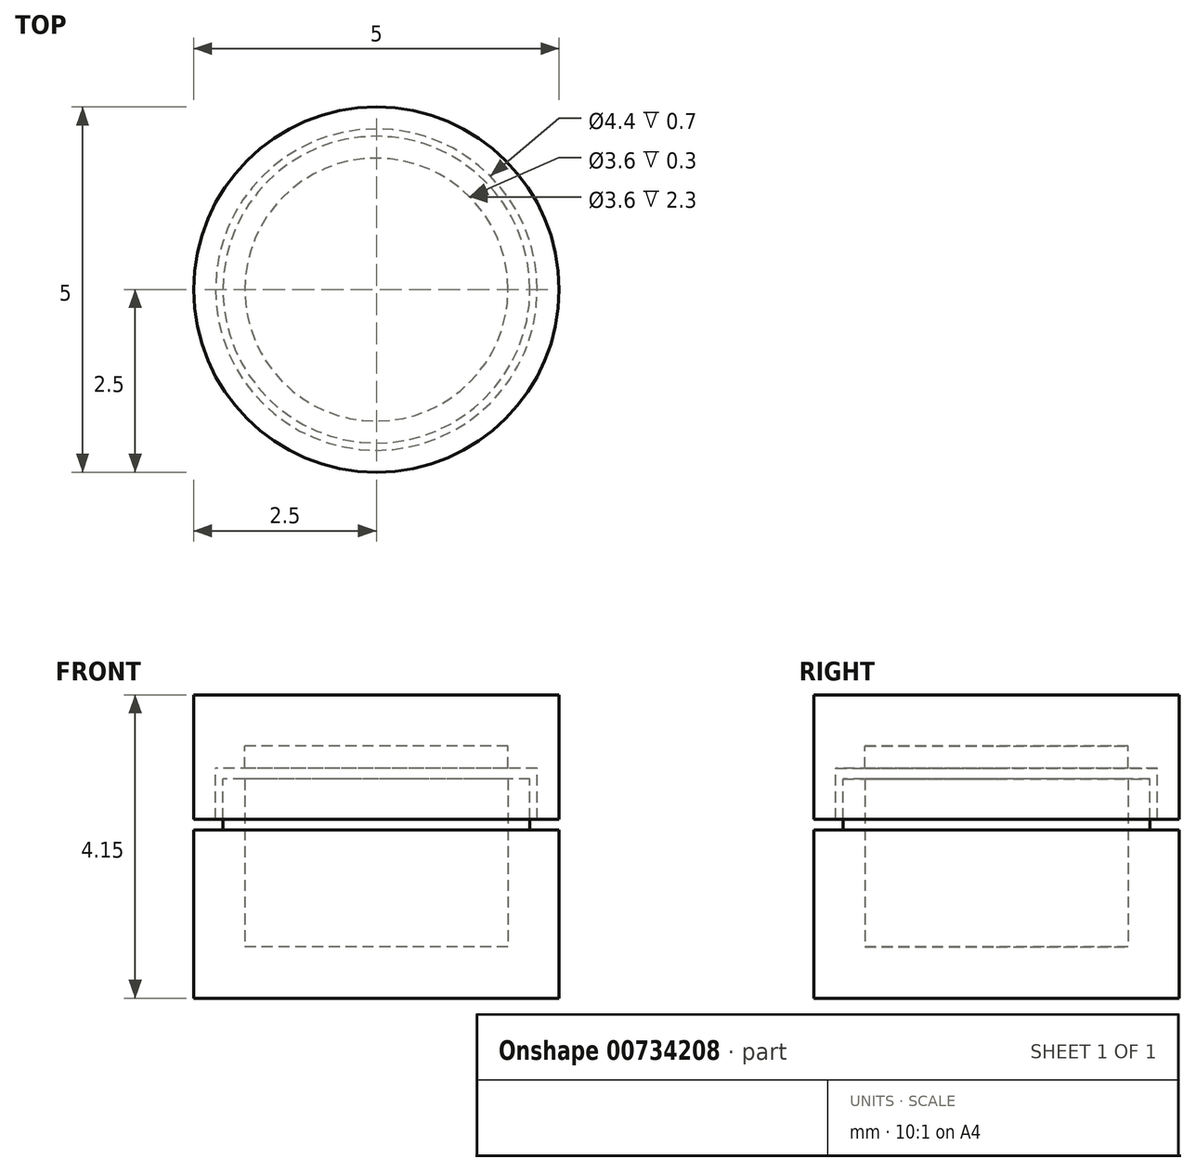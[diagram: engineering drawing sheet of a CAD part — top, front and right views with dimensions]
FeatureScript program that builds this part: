
annotation { "Feature Type Name" : "Feature", "Feature Type Description" : "" }
export const myFeature = defineFeature(function(context is Context, id is Id, definition is map)
    precondition{}
    {
        {
            var Q0;
            Q0=qCreatedBy(makeId("Top.planeOp"),FACE);
            var sketch = newSketch(context, id + "F0", { "sketchPlane" : qUnion([Q0])});
            skCircle(sketch, "E0", {"center": v(0, 0) * mm, "radius": 2.5 * mm});
            skCircle(sketch, "E1", {"center": v(0, 0) * mm, "radius": 1.8 * mm});
            skSolve(sketch);
        }
        {
            var Q0;
            Q0=makeQuery(id+"F0.imprint","IMPRINT",FACE,{"disambiguationData":[TD([[makeQuery(id+"F0.imprint","IMPRINT",EDGE,{"derivedFrom":sQuery(id+"F0.wireOp",EDGE,"E0")}),1.0]])]});
            extrude(context, id + "F1", {"entities" : qUnion([Q0]), "depth" : 3 * mm, "offsetDistance" : 25.4 * mm});
        }
        {
            var Q0;
            Q0=makeQuery(id+"F0.imprint","IMPRINT",FACE,{"disambiguationData":[TD([[makeQuery(id+"F0.imprint","IMPRINT",EDGE,{"derivedFrom":sQuery(id+"F0.wireOp",EDGE,"E1")}),1.0]])]});
            extrude(context, id + "F2", {"entities" : qUnion([Q0]), "operationType" : NewBodyOperationType.ADD, "depth" : 0.7 * mm, "offsetDistance" : 25.4 * mm});
        }
        {
            var Q0;
            Q0=makeQuery(id+"F1.opExtrude","CAP_FACE",FACE,{"disambiguationData":[OSD([sQuery(id+"F0.wireOp",EDGE,"E0"),sQuery(id+"F0.wireOp",EDGE,"E1")])],"isStart":false});
            var sketch = newSketch(context, id + "F3", { "sketchPlane" : qUnion([Q0])});
            skCircle(sketch, "E2.0", {"center": v(0, 0) * mm, "radius": 2.5 * mm});
            skCircle(sketch, "E3", {"center": v(0, 0) * mm, "radius": 2.1 * mm});
            skSolve(sketch);
        }
        {
            var Q0;
            Q0 = qSketchRegion(id + "F3", true);
            extrude(context, id + "F4", {"entities" : qUnion([Q0]), "operationType" : NewBodyOperationType.REMOVE, "oppositeDirection" : true, "depth" : 0.7 * mm, "offsetDistance" : 25.4 * mm});
        }
        {
            var Q0;
            Q0=qCreatedBy(makeId("Front.planeOp"),FACE);
            var sketch = newSketch(context, id + "F5", { "sketchPlane" : qUnion([Q0])});
            skLineSegment(sketch, "E4", {"start": v(-2.5, 2.45) * mm, "end": v(-2.5, 4.15) * mm});
            skLineSegment(sketch, "E5", {"start": v(-2.5, 4.15) * mm, "end": v(0, 4.15) * mm});
            skLineSegment(sketch, "E6", {"start": v(0, 4.15) * mm, "end": v(0, 0) * mm});
            skLineSegment(sketch, "E7", {"start": v(-2.5, 2.45) * mm, "end": v(-2.2, 2.45) * mm});
            skLineSegment(sketch, "E8", {"start": v(-2.2, 2.45) * mm, "end": v(-2.2, 3.15) * mm});
            skLineSegment(sketch, "E9", {"start": v(-2.2, 3.15) * mm, "end": v(-1.8, 3.15) * mm});
            skLineSegment(sketch, "E10", {"start": v(-1.8, 3.15) * mm, "end": v(-1.8, 3.45) * mm});
            skLineSegment(sketch, "E11", {"start": v(-1.8, 3.45) * mm, "end": v(0, 3.45) * mm});
            skSolve(sketch);
        }
        {
            var Q0;
            Q0=makeQuery(id+"F5.imprint","IMPRINT",FACE,{"disambiguationData":[TD([[makeQuery(id+"F5.imprint","IMPRINT",EDGE,{"derivedFrom":sQuery(id+"F5.wireOp",EDGE,"E4")}),-1.0]])]});
            var Q1;
            Q1=sQuery(id+"F5.wireOp",EDGE,"E6");
            revolve(context, id + "F6", {"surfaceOperationType" : NewSurfaceOperationType.NEW, "entities" : qUnion([Q0]), "axis" : qUnion([Q1]), "revolveType" : RevolveType.FULL});
        }
    });
